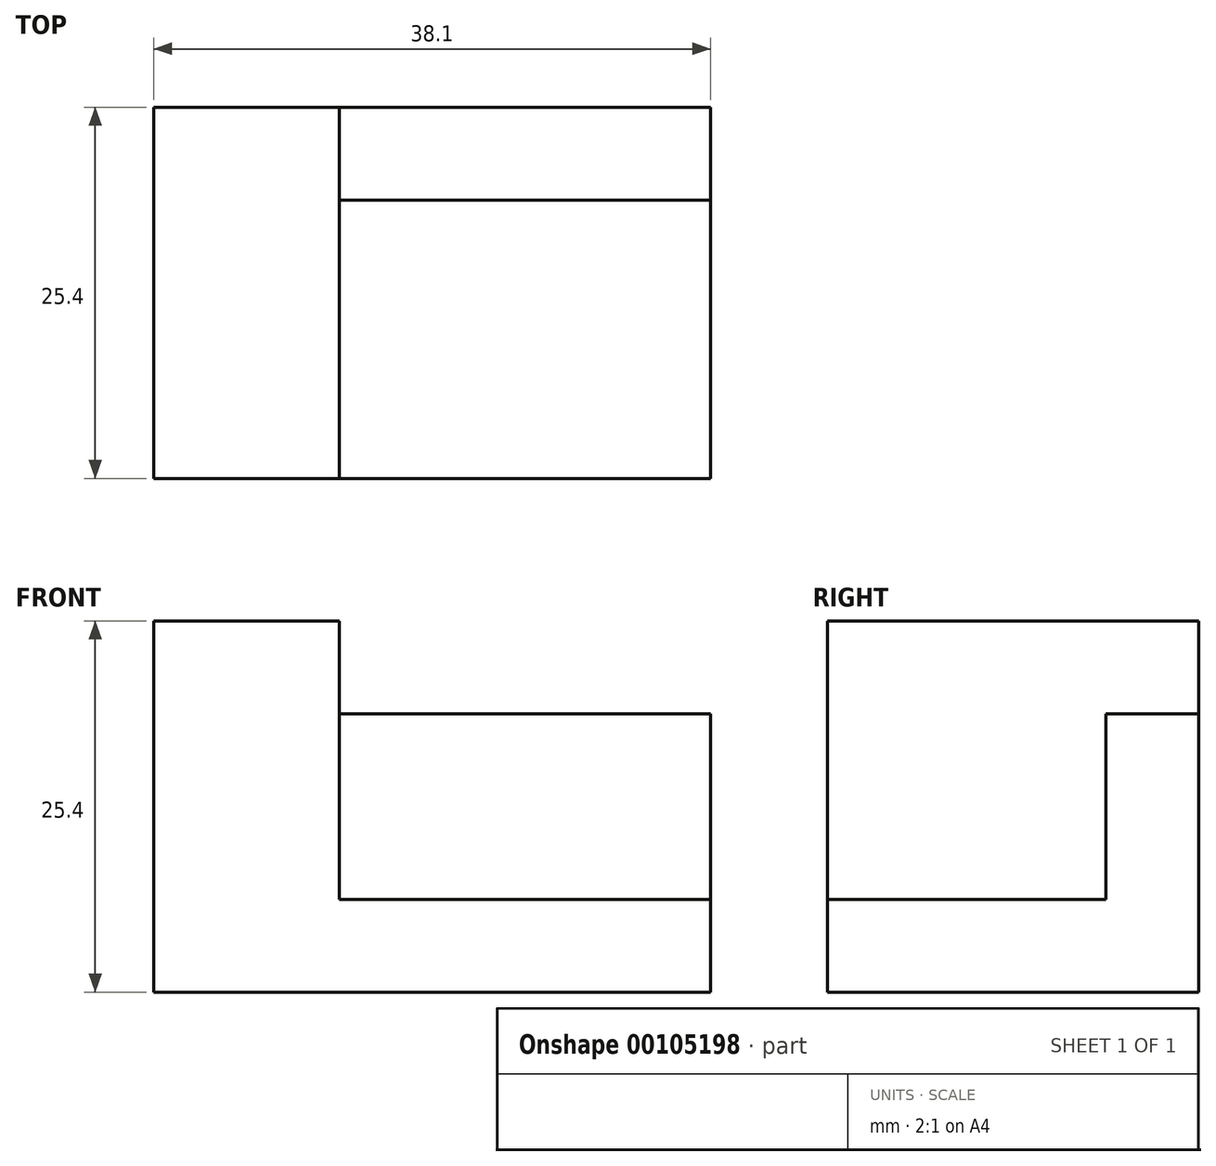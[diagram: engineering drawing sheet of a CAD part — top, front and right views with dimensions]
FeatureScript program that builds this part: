
annotation { "Feature Type Name" : "Feature", "Feature Type Description" : "" }
export const myFeature = defineFeature(function(context is Context, id is Id, definition is map)
    precondition{}
    {
        {
            var Q0;
            Q0=qCreatedBy(makeId("Front.planeOp"),FACE);
            var sketch = newSketch(context, id + "F0", { "sketchPlane" : qUnion([Q0])});
            skLineSegment(sketch, "E0", {"start": v(0, 0) * mm, "end": v(0, 25.4) * mm});
            skLineSegment(sketch, "E1", {"start": v(0, 25.4) * mm, "end": v(12.7, 25.4) * mm});
            skLineSegment(sketch, "E2", {"start": v(12.7, 25.4) * mm, "end": v(12.7, 6.35) * mm});
            skLineSegment(sketch, "E3", {"start": v(12.7, 6.35) * mm, "end": v(38.1, 6.35) * mm});
            skLineSegment(sketch, "E4", {"start": v(38.1, 6.35) * mm, "end": v(38.1, 0) * mm});
            skLineSegment(sketch, "E5", {"start": v(38.1, 0) * mm, "end": v(0, 0) * mm});
            skSolve(sketch);
        }
        {
            var Q0;
            Q0=makeQuery(id+"F0.imprint","IMPRINT",FACE,{"disambiguationData":[TD([[makeQuery(id+"F0.imprint","IMPRINT",EDGE,{"derivedFrom":sQuery(id+"F0.wireOp",EDGE,"E0")}),-1.0]])]});
            extrude(context, id + "F1", {"entities" : qUnion([Q0]), "depth" : 25.4 * mm});
        }
        {
            var Q0;
            Q0=qCreatedBy(makeId("Front.planeOp"),FACE);
            var sketch = newSketch(context, id + "F2", { "sketchPlane" : qUnion([Q0])});
            skLineSegment(sketch, "E6.bottom", {"start": v(38.1, 19.05) * mm, "end": v(12.7, 19.05) * mm});
            skLineSegment(sketch, "E6.top", {"start": v(38.1, 6.35) * mm, "end": v(12.7, 6.35) * mm});
            skLineSegment(sketch, "E6.left", {"start": v(38.1, 19.05) * mm, "end": v(38.1, 6.35) * mm});
            skLineSegment(sketch, "E6.right", {"start": v(12.7, 19.05) * mm, "end": v(12.7, 6.35) * mm});
            skSolve(sketch);
        }
        {
            var Q0;
            Q0 = qSketchRegion(id + "F2", true);
            extrude(context, id + "F3", {"entities" : qUnion([Q0]), "operationType" : NewBodyOperationType.ADD, "depth" : 6.35 * mm});
        }
    });
